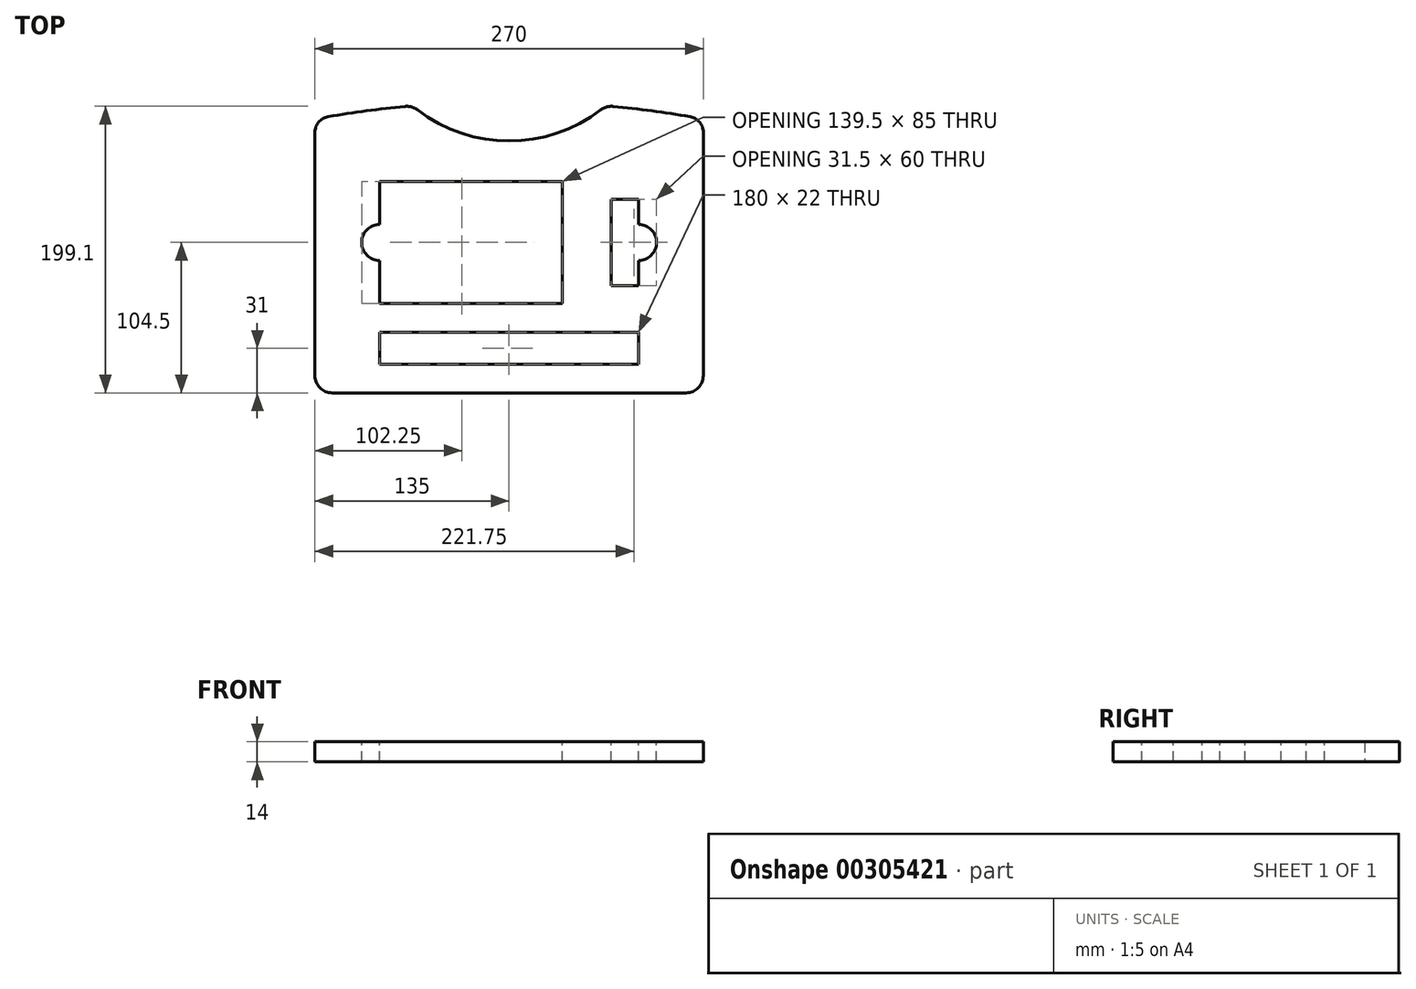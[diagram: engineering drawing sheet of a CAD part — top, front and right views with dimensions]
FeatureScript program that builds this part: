
annotation { "Feature Type Name" : "Feature", "Feature Type Description" : "" }
export const myFeature = defineFeature(function(context is Context, id is Id, definition is map)
    precondition{}
    {
        {
            var Q0;
            Q0=qCreatedBy(makeId("Top.planeOp"),FACE);
            var sketch = newSketch(context, id + "F0", { "sketchPlane" : qUnion([Q0])});
            skLineSegment(sketch, "E0.top", {"start": v(-123, -99.75) * mm, "end": v(123, -99.75) * mm});
            skLineSegment(sketch, "E0.left", {"start": v(-135, 81.33) * mm, "end": v(-135, -87.75) * mm});
            skLineSegment(sketch, "E0.right", {"start": v(135, 81.33) * mm, "end": v(135, -87.75) * mm});
            skLineSegment(sketch, "E1", {"start": v(-173.86, 75.25) * mm, "end": v(164.52, 75.25) * mm, "construction": true});
            skLineSegment(sketch, "E2", {"start": v(-50.1, 180.15) * mm, "end": v(39.06, 180.15) * mm, "construction": true});
            skLineSegment(sketch, "E3", {"start": v(39.06, 180.15) * mm, "end": v(39.06, 177.86) * mm});
            skLineSegment(sketch, "E4", {"start": v(0, 0) * mm, "end": v(0, 180.15) * mm, "construction": true});
            skArc(sketch, "E5", {"start": v(0, 75.25) * mm, "mid": v(-33.68, 80.8) * mm, "end": v(-63.8, 96.88) * mm});
            skArc(sketch, "E6", {"start": v(0, 75.25) * mm, "mid": v(33.68, 80.8) * mm, "end": v(63.8, 96.88) * mm});
            skPoint(sketch, "E7", {"position": v(0, -649.75) * mm});
            skArc(sketch, "E8", {"start": v(125.84, 92.18) * mm, "mid": v(99.1, 96.22) * mm, "end": v(72.24, 99.3) * mm});
            skArc(sketch, "E9.trimOffspring", {"start": v(-72.24, 99.3) * mm, "mid": v(-99.1, 96.22) * mm, "end": v(-125.84, 92.18) * mm});
            skPoint(sketch, "E10.visualSharp", {"position": v(67.38, 99.75) * mm});
            skArc(sketch, "E10.filletArc", {"start": v(72.24, 99.3) * mm, "mid": v(67.8, 98.89) * mm, "end": v(63.8, 96.88) * mm});
            skPoint(sketch, "E11.visualSharp", {"position": v(-67.38, 99.75) * mm});
            skArc(sketch, "E11.filletArc", {"start": v(-63.8, 96.88) * mm, "mid": v(-67.8, 98.89) * mm, "end": v(-72.24, 99.3) * mm});
            skPoint(sketch, "E12.visualSharp", {"position": v(-135, 90.56) * mm});
            skArc(sketch, "E12.filletArc", {"start": v(-125.84, 92.18) * mm, "mid": v(-132.4, 88.43) * mm, "end": v(-135, 81.33) * mm});
            skPoint(sketch, "E13.visualSharp", {"position": v(135, 90.56) * mm});
            skArc(sketch, "E13.filletArc", {"start": v(135, 81.33) * mm, "mid": v(132.4, 88.43) * mm, "end": v(125.84, 92.18) * mm});
            skPoint(sketch, "E14.visualSharp", {"position": v(135, -99.75) * mm});
            skArc(sketch, "E14.filletArc", {"start": v(123, -99.75) * mm, "mid": v(131.49, -96.24) * mm, "end": v(135, -87.75) * mm});
            skPoint(sketch, "E15.visualSharp", {"position": v(-135, -99.75) * mm});
            skArc(sketch, "E15.filletArc", {"start": v(-135, -87.75) * mm, "mid": v(-131.49, -96.24) * mm, "end": v(-123, -99.75) * mm});
            skSolve(sketch);
        }
        {
            var Q0;
            Q0 = qSketchRegion(id + "F0", true);
            extrude(context, id + "F1", {"entities" : qUnion([Q0]), "depth" : 14 * mm});
        }
        {
            var Q0;
            Q0=makeQuery(id+"F1.opExtrude","CAP_FACE",FACE,{"disambiguationData":[OSD([sQuery(id+"F0.wireOp",EDGE,"E0.top"),sQuery(id+"F0.wireOp",EDGE,"E0.left"),sQuery(id+"F0.wireOp",EDGE,"E0.right"),sQuery(id+"F0.wireOp",EDGE,"E5"),sQuery(id+"F0.wireOp",EDGE,"E6"),sQuery(id+"F0.wireOp",EDGE,"E8"),sQuery(id+"F0.wireOp",EDGE,"E9.trimOffspring"),sQuery(id+"F0.wireOp",EDGE,"E10.filletArc"),sQuery(id+"F0.wireOp",EDGE,"E11.filletArc"),sQuery(id+"F0.wireOp",EDGE,"E12.filletArc"),sQuery(id+"F0.wireOp",EDGE,"E13.filletArc"),sQuery(id+"F0.wireOp",EDGE,"E14.filletArc"),sQuery(id+"F0.wireOp",EDGE,"E15.filletArc")])],"isStart":false});
            var sketch = newSketch(context, id + "F2", { "sketchPlane" : qUnion([Q0])});
            skLineSegment(sketch, "E16.bottom", {"start": v(-90, 47.25) * mm, "end": v(37, 47.25) * mm});
            skLineSegment(sketch, "E16.top", {"start": v(-90, -37.75) * mm, "end": v(37, -37.75) * mm});
            skLineSegment(sketch, "E16.left", {"start": v(-90, 47.25) * mm, "end": v(-90, -37.75) * mm});
            skLineSegment(sketch, "E16.right", {"start": v(37, 47.25) * mm, "end": v(37, -37.75) * mm});
            skLineSegment(sketch, "E17.bottom", {"start": v(-90, -57.75) * mm, "end": v(90, -57.75) * mm});
            skLineSegment(sketch, "E17.top", {"start": v(-90, -79.75) * mm, "end": v(90, -79.75) * mm});
            skLineSegment(sketch, "E17.left", {"start": v(-90, -57.75) * mm, "end": v(-90, -79.75) * mm});
            skLineSegment(sketch, "E17.right", {"start": v(90, -57.75) * mm, "end": v(90, -79.75) * mm});
            skLineSegment(sketch, "E18", {"start": v(-26.5, -37.75) * mm, "end": v(-26.5, -111.98) * mm, "construction": true});
            skLineSegment(sketch, "E19", {"start": v(-26.5, -111.98) * mm, "end": v(-24.86, -111.98) * mm, "construction": true});
            skLineSegment(sketch, "E20.bottom", {"start": v(71, 34.75) * mm, "end": v(90, 34.75) * mm});
            skLineSegment(sketch, "E20.top", {"start": v(71, -25.25) * mm, "end": v(90, -25.25) * mm});
            skLineSegment(sketch, "E20.left", {"start": v(71, 34.75) * mm, "end": v(71, -25.25) * mm});
            skLineSegment(sketch, "E20.right", {"start": v(90, 34.75) * mm, "end": v(90, -25.25) * mm});
            skLineSegment(sketch, "E21", {"start": v(37, 4.75) * mm, "end": v(108.53, 4.75) * mm, "construction": true});
            skSolve(sketch);
        }
        {
            var Q0;
            Q0 = qSketchRegion(id + "F2", true);
            extrude(context, id + "F3", {"entities" : qUnion([Q0]), "operationType" : NewBodyOperationType.REMOVE, "oppositeDirection" : true, "depth" : 25 * mm});
        }
        {
            var Q0;
            Q0=makeQuery(id+"F1.opExtrude","CAP_FACE",FACE,{"disambiguationData":[OSD([sQuery(id+"F0.wireOp",EDGE,"E0.top"),sQuery(id+"F0.wireOp",EDGE,"E0.left"),sQuery(id+"F0.wireOp",EDGE,"E0.right"),sQuery(id+"F0.wireOp",EDGE,"E5"),sQuery(id+"F0.wireOp",EDGE,"E6"),sQuery(id+"F0.wireOp",EDGE,"E8"),sQuery(id+"F0.wireOp",EDGE,"E9.trimOffspring"),sQuery(id+"F0.wireOp",EDGE,"E10.filletArc"),sQuery(id+"F0.wireOp",EDGE,"E11.filletArc"),sQuery(id+"F0.wireOp",EDGE,"E12.filletArc"),sQuery(id+"F0.wireOp",EDGE,"E13.filletArc"),sQuery(id+"F0.wireOp",EDGE,"E14.filletArc"),sQuery(id+"F0.wireOp",EDGE,"E15.filletArc")])],"isStart":false});
            var sketch = newSketch(context, id + "F4", { "sketchPlane" : qUnion([Q0])});
            skCircle(sketch, "E22", {"center": v(-90, 4.75) * mm, "radius": 12.5 * mm});
            skCircle(sketch, "E23", {"center": v(90, 4.75) * mm, "radius": 12.5 * mm});
            skSolve(sketch);
        }
        {
            var Q0;
            Q0 = qSketchRegion(id + "F4", true);
            extrude(context, id + "F5", {"entities" : qUnion([Q0]), "operationType" : NewBodyOperationType.REMOVE, "oppositeDirection" : true, "depth" : 25 * mm});
        }
    });
